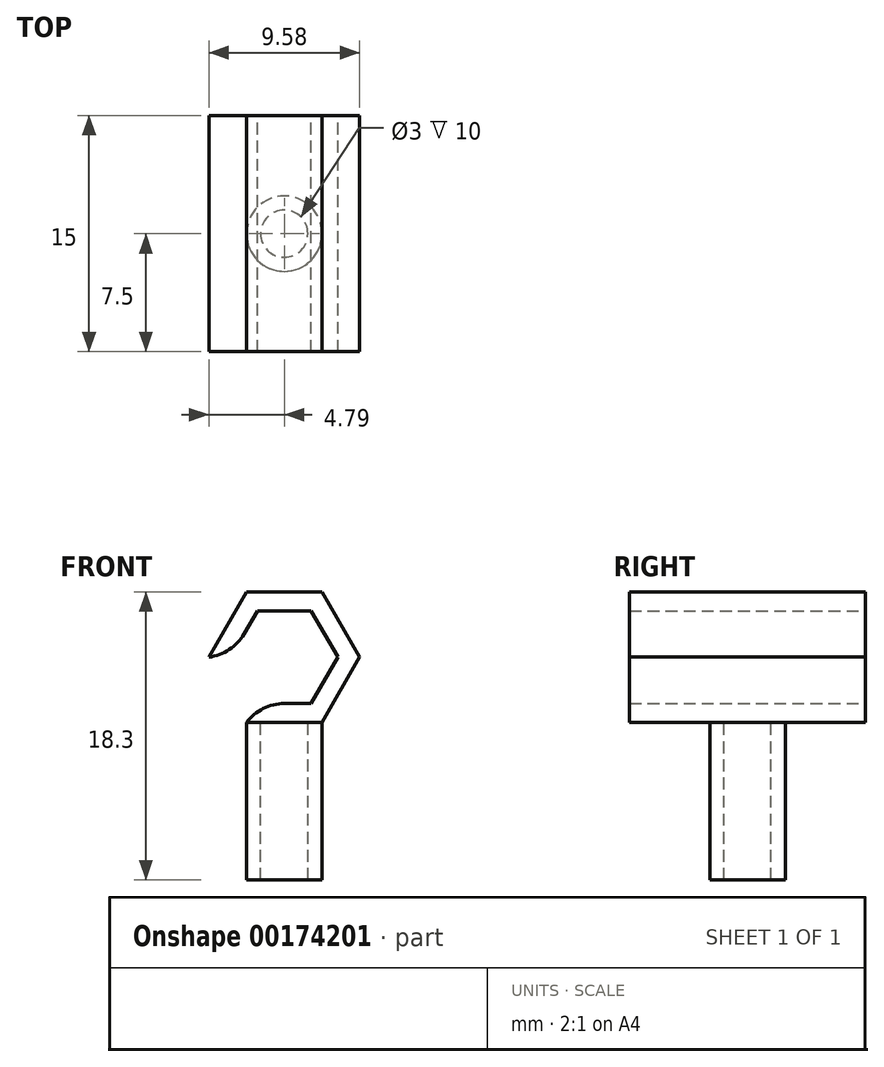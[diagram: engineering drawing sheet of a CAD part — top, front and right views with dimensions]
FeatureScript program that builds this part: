
annotation { "Feature Type Name" : "Feature", "Feature Type Description" : "" }
export const myFeature = defineFeature(function(context is Context, id is Id, definition is map)
    precondition{}
    {
        {
            var Q0;
            Q0=qCreatedBy(makeId("Front.planeOp"),FACE);
            var sketch = newSketch(context, id + "F0", { "sketchPlane" : qUnion([Q0])});
            skCircle(sketch, "E0.cCircle", {"center": v(0, 0) * mm, "radius": 2.95 * mm, "construction": true});
            skLineSegment(sketch, "E0.0", {"start": v(-1.7, 2.95) * mm, "end": v(1.7, 2.95) * mm});
            skLineSegment(sketch, "E0.1", {"start": v(1.7, 2.95) * mm, "end": v(3.4, 0) * mm});
            skLineSegment(sketch, "E0.2", {"start": v(3.4, 0) * mm, "end": v(1.7, -2.95) * mm});
            skLineSegment(sketch, "E0.3", {"start": v(1.7, -2.95) * mm, "end": v(-1.7, -2.95) * mm});
            skLineSegment(sketch, "E0.4", {"start": v(-1.7, -2.95) * mm, "end": v(-3.4, 0) * mm});
            skLineSegment(sketch, "E0.5", {"start": v(-3.4, 0) * mm, "end": v(-1.7, 2.95) * mm});
            skPoint(sketch, "E0.0.midPoint", {"position": v(0, 2.95) * mm});
            skCircle(sketch, "E1.cCircle", {"center": v(0, 0) * mm, "radius": 4.15 * mm, "construction": true});
            skLineSegment(sketch, "E1.0", {"start": v(-2.4, 4.15) * mm, "end": v(2.4, 4.15) * mm});
            skLineSegment(sketch, "E1.1", {"start": v(2.4, 4.15) * mm, "end": v(4.8, 0) * mm});
            skLineSegment(sketch, "E1.2", {"start": v(4.8, 0) * mm, "end": v(2.4, -4.15) * mm});
            skLineSegment(sketch, "E1.3", {"start": v(2.4, -4.15) * mm, "end": v(-2.4, -4.15) * mm});
            skLineSegment(sketch, "E1.4", {"start": v(-2.4, -4.15) * mm, "end": v(-4.8, 0) * mm});
            skLineSegment(sketch, "E1.5", {"start": v(-4.8, 0) * mm, "end": v(-2.4, 4.15) * mm});
            skPoint(sketch, "E1.0.midPoint", {"position": v(0, 4.15) * mm});
            skLineSegment(sketch, "E2", {"start": v(-3.4, 0) * mm, "end": v(-4.8, 0) * mm});
            skLineSegment(sketch, "E3", {"start": v(-1.7, -2.95) * mm, "end": v(-2.4, -4.15) * mm});
            skSolve(sketch);
        }
        {
            var Q0;
            Q0=makeQuery(id+"F0.imprint","IMPRINT",FACE,{"disambiguationData":[TD([[makeQuery(id+"F0.imprint","IMPRINT",EDGE,{"derivedFrom":sQuery(id+"F0.wireOp",EDGE,"E0.0")}),1.0]])]});
            extrude(context, id + "F1", {"entities" : qUnion([Q0]), "depth" : 15 * mm});
        }
        {
            var Q0;
            Q0=makeQuery(id+"F1.opExtrude","SWEPT_EDGE",EDGE,{"disambiguationData":[OSD([sQuery(id+"F0.wireOp",EDGE,"E0.4"),sQuery(id+"F0.wireOp",EDGE,"E0.5"),sQuery(id+"F0.wireOp",EDGE,"E2")])]});
            var Q1;
            Q1=makeQuery(id+"F1.opExtrude","SWEPT_EDGE",EDGE,{"disambiguationData":[OSD([sQuery(id+"F0.wireOp",EDGE,"E0.3"),sQuery(id+"F0.wireOp",EDGE,"E0.4"),sQuery(id+"F0.wireOp",EDGE,"E3")])]});
            fillet(context, id + "F2", {"entities" : qUnion([Q0, Q1]), "radius" : 3 * mm, "tangentPropagation" : true, "allowEdgeOverflow" : false});
        }
        {
            var Q0;
            Q0=makeQuery(id+"F1.opExtrude","SWEPT_FACE",FACE,{"disambiguationData":[OSD([sQuery(id+"F0.wireOp",EDGE,"E1.3")])]});
            var sketch = newSketch(context, id + "F3", { "sketchPlane" : qUnion([Q0])});
            skLineSegment(sketch, "E4", {"start": v(2.4, 7.5) * mm, "end": v(-2.4, 7.5) * mm, "construction": true});
            skCircle(sketch, "E5", {"center": v(0, 7.5) * mm, "radius": 2.4 * mm});
            skCircle(sketch, "E6", {"center": v(0, 7.5) * mm, "radius": 1.5 * mm});
            skSolve(sketch);
        }
        {
            var Q0;
            Q0=makeQuery(id+"F3.imprint","IMPRINT",FACE,{"disambiguationData":[TD([[makeQuery(id+"F3.imprint","IMPRINT",EDGE,{"derivedFrom":sQuery(id+"F3.wireOp",EDGE,"E6")}),-1.0]])]});
            var Q1;
            Q1=sQuery(id+"F3.wireOp",EDGE,"E5");
            var Q2;
            Q2=sQuery(id+"F3.wireOp",EDGE,"E6");
            extrude(context, id + "F4", {"entities" : qUnion([Q0]), "operationType" : NewBodyOperationType.ADD, "surfaceEntities" : qUnion([Q1, Q2]), "depth" : 10 * mm});
        }
    });
